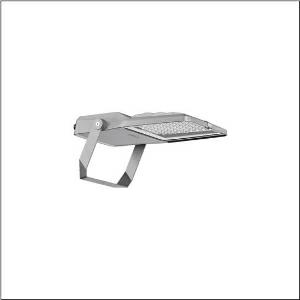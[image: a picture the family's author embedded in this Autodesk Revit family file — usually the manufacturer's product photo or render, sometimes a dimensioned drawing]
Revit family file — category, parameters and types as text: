
# Revit family: floodlight_fl_21_iq_mini___pl64_5xa7772d1e1a_af72
name_source: partatom
category: Lighting Fixtures
units: mm (PartAtom-declared; Revit-internal decimal feet)

## family parameters
Cut with Voids When Loaded = No
Host = Face
Light Source = No
Part Type = Normal
Room Calculation Point = No
Round Connector Dimension = Use Diameter
Shared = No

## types (1)
- --- (1 x LED, 14250 lm, 143 W, 2200K)
    Apparent Load = 143 VA
    CIE Flux Codes = 28 80 98 100 100
    Color Rendering = 70
    Color Temperature = 2200K
    Default Elevation = 1800 mm
    Description = Floodlight FL 21 iQ mini, floodlight, primary light control with lens, of PMMA, primary optical cover: protective disc, of toughened safety glass, transparent, light distribution: PL64, light emission: direct distribution, installation type: surface-mounted, lamps: LED, High Power LED, rated values: 14.250lm | 143W | 99,7lm/W (begin service life); end service life: 14.250lm | 151,6W; at 50% lumin. flux: 7.125lm | 60,5W | 117,8lm/W, colour temperature: 2200K, colour rendering: CRI > 70, light colour: 722, light setting 1 begin service life: 100% | 14.250lm | 143W | 99,7lm/W | 2.200K, light setting 1 end service life: 151,6W, further light settings possible, control: Street-Remote, Auto-Match, Temp-Guard, Night-Set, Smart-Wire, Desk-Remote (wireless, voltage-free reading and setting of iQ features in the workshop via application-optimized NFC function/RFID function), optimised constant luminous flux control (CLO 2.0), pre-setting: linear dimming characteristic, with terminal, 6-pole, mains connection: 220..240V, AC, 50/60Hz, luminaire housing, of diecast aluminium, powder-coated, SITECO metallic grey (DB 702S), corrosivity category C5 mid according to DIN EN ISO 12944suitable for swimming poolschlorine-resistant, sealing non-destructively replaceable, mounting bracket, of steel, galvanised, powder-coated, SITECO metallic grey (DB 702S), protection rating (complete): IP66, insulation class (complete): insulation class II (safety insulation), certification: CE, ENEC, VDE, protection symbol: D, impact resistance: IK08, permissible operating ambient temperature: -40..+40°C, permissible operating ambient temperature for outdoor applications: -40..+50°C, standard: DIN EN 12944, LABS conformity tested according to VDMA 24364:2018-05, packaging unit: 1 piece

Light Distribution: PL64
    Height = 70 mm
    Lamp = 1 x LED
    Lamp Light Flux = 14250 lm
    Lamp Power = 143 W
    Lamp count = 1
    Length = 485 mm
    Luminous efficacy = 100 lm/W
    Manufacturer = Siteco
    ModVariant = No
    Model = 5XA7772D1E1A
    Number of Poles = 1
    OnlyDefault = Yes
    Power Factor = 1
    Product Name = Floodlight FL 21 iQ mini | PL64
    Product group = floodlight | pylon annexe
    ProductGroupID = 6201
    Protection Class = Protection class II
    Protection Degree = IP 66
    RLX_Detail_Level = 1
    RLX_Emergency_Light_Flux = 0 lm
    RLX_Emergency_Type = 0
    RLX_Emergency_Type_DB = No
    RlxData = <blob elided: 96689 chars, md5=2abab869>
    Socket = socket
    Standby Power = 0 W
    System Light Flux = 14250 lm
    System Power = 143 W
    Type Comments = factory setting: luminous flux: 100 % | dim-lin: 254 | 730 mA
    Type Image = l_1006845.jpg
    URL = http://relux.com
    VarID = @adj_165393
    Voltage = 0 V
    Weight = 0.00 kg
    Width = 337 mm

## geometry (parser evidence)
native form markers: Blend x4, Sweep x11
no freeform markers — native parametric forms only
